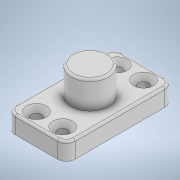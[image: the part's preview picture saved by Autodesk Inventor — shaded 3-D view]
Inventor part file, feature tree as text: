
AUTODESK INVENTOR PART (.ipt)
format: ipt  version: 2020.3 (Build 243373000, 373)  size: 176,128 bytes
history: native  units: mm
features: extrude x3, sketch x2, fillet x2, hole x1
ambient origin geometry x8: Origin, YZ Plane, XZ Plane, XY Plane, X Axis, Y Axis, Z Axis, Center Point
bodies: Solid1 (feature_tree)
feature tree (8):
  sketch  "Sketch1"  dims[d0=24.6mm d1=12.4mm]
  extrude  "Extrusion1"  Depth=12.4mm
  extrude  "Extrusion2"  Depth=2.0mm
  fillet  "Fillet1"  Radius=4.0mm
  extrude  "Extrusion3"  Depth=4.0mm TaperAngle=0.0deg
  fillet  "Fillet2"  Radius=2.0mm
  hole  "Hole2"  [1 undecoded]
  sketch  "Sketch3"  dims[d2=6.0mm d4=6.0mm d5=4.0mm d6=0.0mm d7=4.0mm d8=0.0mm d16=2.0mm d17=8.5mm d18=10.3mm d19=0.0mm d20=0.5mm d21=6.8mm d28=2.3mm d29=6.0mm d30=4.5mm d31=2.0mm d32=90.0deg d33=6.5mm d34=0.0mm]
note: 1 required parameter value undecoded (feature->parameter linkage not recoverable at this tier; creation-order binding heuristic only, values carry confidence <= 0.55)
